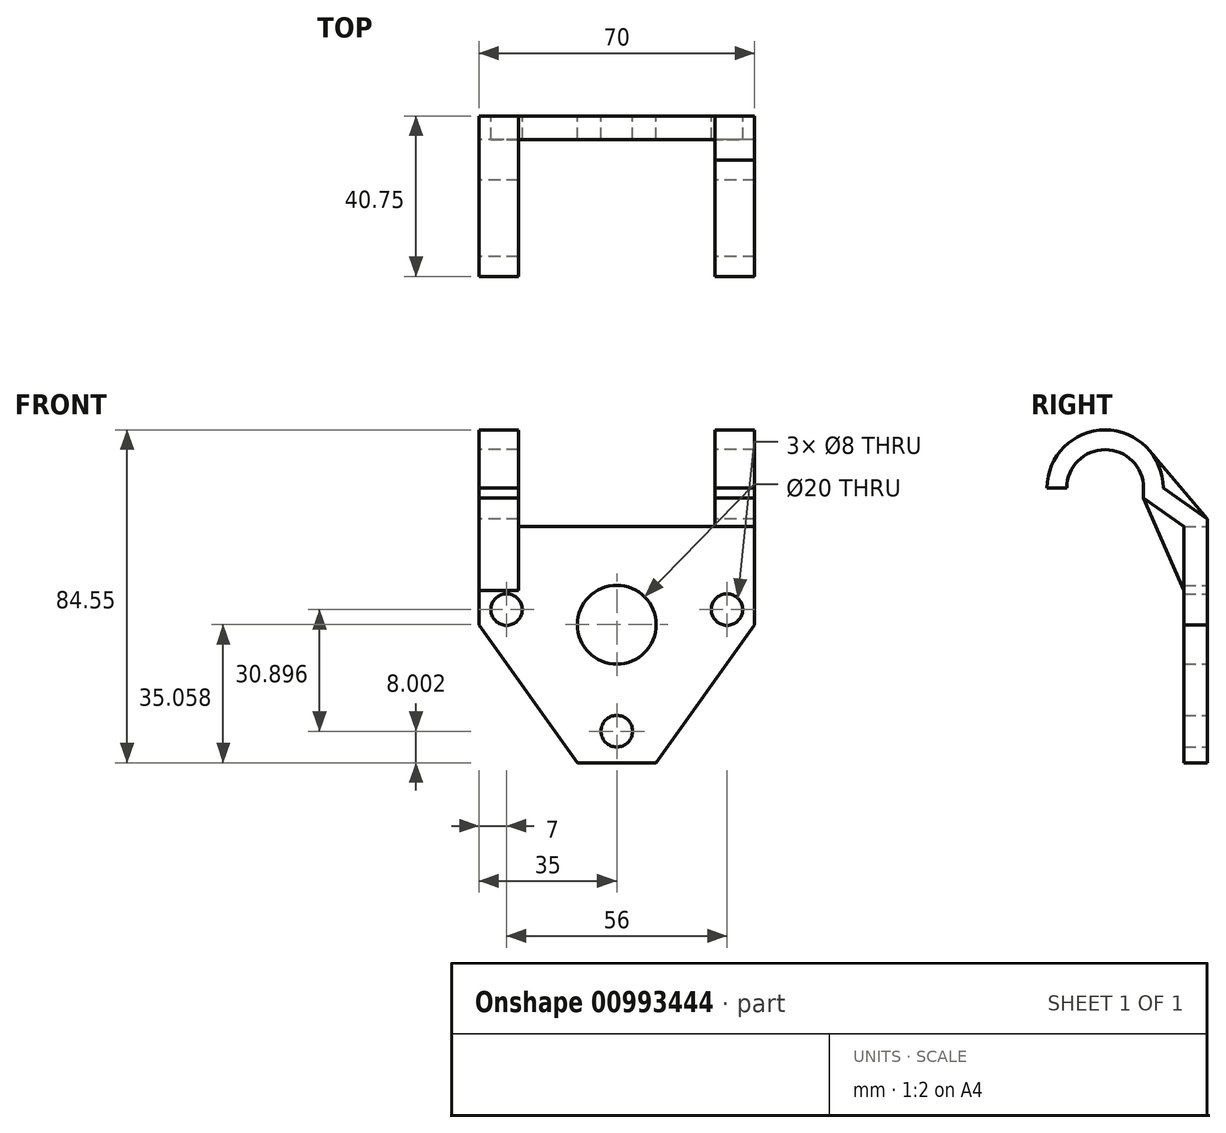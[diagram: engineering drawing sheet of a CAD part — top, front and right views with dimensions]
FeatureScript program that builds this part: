
annotation { "Feature Type Name" : "Feature", "Feature Type Description" : "" }
export const myFeature = defineFeature(function(context is Context, id is Id, definition is map)
    precondition{}
    {
        {
            var Q0;
            Q0=qCreatedBy(makeId("Right.planeOp"),FACE);
            var sketch = newSketch(context, id + "F0", { "sketchPlane" : qUnion([Q0])});
            skArc(sketch, "E0", {"start": v(9.75, 0) * mm, "mid": v(0, 9.75) * mm, "end": v(-9.75, 0) * mm});
            skArc(sketch, "E1.0", {"start": v(14.75, 0) * mm, "mid": v(0, 14.75) * mm, "end": v(-14.75, 0) * mm});
            skLineSegment(sketch, "E2.trimOffspring", {"start": v(-9.75, 0) * mm, "end": v(-14.75, 0) * mm});
            skPoint(sketch, "E3", {"position": v(0, 14.75) * mm});
            skLineSegment(sketch, "E4", {"start": v(14.75, 0) * mm, "end": v(26, -7.9) * mm});
            skLineSegment(sketch, "E5", {"start": v(9.75, -2.6) * mm, "end": v(20, -9.8) * mm});
            skLineSegment(sketch, "E6", {"start": v(9.75, -2.6) * mm, "end": v(9.75, 0) * mm});
            skLineSegment(sketch, "E7", {"start": v(20, -9.8) * mm, "end": v(20, -69.8) * mm});
            skLineSegment(sketch, "E8", {"start": v(26, -7.9) * mm, "end": v(26, -69.8) * mm});
            skLineSegment(sketch, "E9", {"start": v(20, -69.8) * mm, "end": v(26, -69.8) * mm});
            skSolve(sketch);
        }
        {
            var Q0;
            Q0 = qSketchRegion(id + "F0", true);
            extrude(context, id + "F1", {"entities" : qUnion([Q0]), "depth" : 70 * mm, "offsetDistance" : 25 * mm});
        }
        {
            var Q0;
            Q0=makeQuery(id+"F1.opExtrude","CAP_FACE",FACE,{"disambiguationData":[OSD([sQuery(id+"F0.wireOp",EDGE,"E0"),sQuery(id+"F0.wireOp",EDGE,"E1.0"),sQuery(id+"F0.wireOp",EDGE,"E2.trimOffspring"),sQuery(id+"F0.wireOp",EDGE,"E4"),sQuery(id+"F0.wireOp",EDGE,"E5"),sQuery(id+"F0.wireOp",EDGE,"E6"),sQuery(id+"F0.wireOp",EDGE,"E7"),sQuery(id+"F0.wireOp",EDGE,"E8"),sQuery(id+"F0.wireOp",EDGE,"E9")])],"isStart":false});
            var sketch = newSketch(context, id + "F2", { "sketchPlane" : qUnion([Q0])});
            skPoint(sketch, "E10", {"position": v(0, 14.75) * mm});
            skSolve(sketch);
        }
        {
            var Q0;
            Q0=makeQuery(id+"F1.opExtrude","CAP_FACE",FACE,{"disambiguationData":[OSD([sQuery(id+"F0.wireOp",EDGE,"E0"),sQuery(id+"F0.wireOp",EDGE,"E1.0"),sQuery(id+"F0.wireOp",EDGE,"E2.trimOffspring"),sQuery(id+"F0.wireOp",EDGE,"E4"),sQuery(id+"F0.wireOp",EDGE,"E5"),sQuery(id+"F0.wireOp",EDGE,"E6"),sQuery(id+"F0.wireOp",EDGE,"E7"),sQuery(id+"F0.wireOp",EDGE,"E8"),sQuery(id+"F0.wireOp",EDGE,"E9")])],"isStart":true});
            var sketch = newSketch(context, id + "F3", { "sketchPlane" : qUnion([Q0])});
            skPoint(sketch, "E11", {"position": v(0, 14.75) * mm});
            skSolve(sketch);
        }
        {
            var Q0;
            Q0=makeQuery(id+"F1.opExtrude","SWEPT_FACE",FACE,{"disambiguationData":[OSD([sQuery(id+"F0.wireOp",EDGE,"E8")])]});
            var sketch = newSketch(context, id + "F4", { "sketchPlane" : qUnion([Q0])});
            skLineSegment(sketch, "E12", {"start": v(-70, -34.8) * mm, "end": v(-45, -69.8) * mm});
            skLineSegment(sketch, "E13", {"start": v(-45, -69.8) * mm, "end": v(-25, -69.8) * mm});
            skLineSegment(sketch, "E14", {"start": v(-25, -69.8) * mm, "end": v(0, -34.8) * mm});
            skLineSegment(sketch, "E15", {"start": v(-70, -34.8) * mm, "end": v(-90, -34.8) * mm});
            skLineSegment(sketch, "E16", {"start": v(-90, -34.8) * mm, "end": v(-90, -94.8) * mm});
            skLineSegment(sketch, "E17", {"start": v(-90, -94.8) * mm, "end": v(20, -94.8) * mm});
            skLineSegment(sketch, "E18", {"start": v(20, -94.8) * mm, "end": v(20, -34.8) * mm});
            skLineSegment(sketch, "E19", {"start": v(20, -34.8) * mm, "end": v(0, -34.8) * mm});
            skLineSegment(sketch, "E20", {"start": v(-60, -9.8) * mm, "end": v(-10, -9.8) * mm});
            skLineSegment(sketch, "E21", {"start": v(-60, -9.8) * mm, "end": v(-60, 14.75) * mm});
            skLineSegment(sketch, "E22", {"start": v(-60, 14.75) * mm, "end": v(-10, 14.75) * mm});
            skLineSegment(sketch, "E23", {"start": v(-10, 14.75) * mm, "end": v(-10, -9.8) * mm});
            skSolve(sketch);
        }
        {
            var Q0;
            Q0 = qSketchRegion(id + "F4", true);
            extrude(context, id + "F5", {"entities" : qUnion([Q0]), "operationType" : NewBodyOperationType.REMOVE, "oppositeDirection" : true, "depth" : 25 * mm, "offsetDistance" : 25 * mm});
        }
        {
            var Q0;
            Q0=makeQuery(id+"F1.opExtrude","SWEPT_FACE",FACE,{"disambiguationData":[OSD([sQuery(id+"F0.wireOp",EDGE,"E8")])]});
            var sketch = newSketch(context, id + "F6", { "sketchPlane" : qUnion([Q0])});
            skCircle(sketch, "E24", {"center": v(-63, -30.9) * mm, "radius": 4 * mm});
            skCircle(sketch, "E25", {"center": v(-7, -30.9) * mm, "radius": 4 * mm});
            skSolve(sketch);
        }
        {
            var Q0;
            Q0 = qSketchRegion(id + "F4", true);
            extrude(context, id + "F7", {"entities" : qUnion([Q0]), "operationType" : NewBodyOperationType.REMOVE, "endBound" : BoundingType.THROUGH_ALL, "oppositeDirection" : true, "depth" : 25 * mm, "offsetDistance" : 25 * mm});
        }
        {
            var Q0;
            Q0=makeQuery(id+"F6.imprint","IMPRINT",FACE,{"disambiguationData":[TD([[makeQuery(id+"F6.imprint","IMPRINT",EDGE,{"derivedFrom":sQuery(id+"F6.wireOp",EDGE,"E25")}),-1.0]])]});
            var sketch = newSketch(context, id + "F8", { "sketchPlane" : qUnion([Q0])});
            skCircle(sketch, "E26", {"center": v(-35, -34.74) * mm, "radius": 10 * mm});
            skSolve(sketch);
        }
        {
            var Q0;
            Q0 = qSketchRegion(id + "F8", true);
            extrude(context, id + "F9", {"entities" : qUnion([Q0]), "operationType" : NewBodyOperationType.REMOVE, "endBound" : BoundingType.THROUGH_ALL, "oppositeDirection" : true, "depth" : 2.5 * mm, "offsetDistance" : 25 * mm});
        }
        {
            var Q0;
            Q0=makeQuery(id+"F6.imprint","IMPRINT",FACE,{"disambiguationData":[TD([[makeQuery(id+"F6.imprint","IMPRINT",EDGE,{"derivedFrom":sQuery(id+"F6.wireOp",EDGE,"E25")}),-1.0]])]});
            var sketch = newSketch(context, id + "F10", { "sketchPlane" : qUnion([Q0])});
            skCircle(sketch, "E27", {"center": v(-35, -34.74) * mm, "radius": 6.38 * mm});
            skSolve(sketch);
        }
        {
            var Q0;
            Q0 = qSketchRegion(id + "F10", true);
            extrude(context, id + "F11", {"entities" : qUnion([Q0]), "operationType" : NewBodyOperationType.REMOVE, "endBound" : BoundingType.THROUGH_ALL, "oppositeDirection" : true, "depth" : 25 * mm, "offsetDistance" : 25 * mm});
        }
        {
            var Q0;
            Q0 = qSketchRegion(id + "F6", true);
            extrude(context, id + "F12", {"entities" : qUnion([Q0]), "operationType" : NewBodyOperationType.REMOVE, "endBound" : BoundingType.THROUGH_ALL, "oppositeDirection" : true, "depth" : 25 * mm, "offsetDistance" : 25 * mm});
        }
        {
            var Q0;
            Q0=qCreatedBy(makeId("Right.planeOp"),FACE);
            cPlane(context, id + "F13", {"entities" : qUnion([Q0]), "cplaneType" : CPlaneType.OFFSET, "offset" : 35 * mm, "width" : 150 * mm, "height" : 150 * mm});
        }
        {
            var Q0;
            Q0=makeQuery(id+"F3.imprint","IMPRINT",FACE,{"disambiguationData":[TD([[makeQuery(id+"F3.imprint","IMPRINT",EDGE,{"derivedFrom":makeQuery(id+"F1.opExtrude","CAP_EDGE",EDGE,{"disambiguationData":[OSD([sQuery(id+"F0.wireOp",EDGE,"E0")])],"isStart":true})}),1.0]])]});
            var sketch = newSketch(context, id + "F14", { "sketchPlane" : qUnion([Q0])});
            skLineSegment(sketch, "E28", {"start": v(-20, -26) * mm, "end": v(-9.75, -2.6) * mm});
            skLineSegment(sketch, "E29", {"start": v(-9.75, -2.6) * mm, "end": v(-20, -9.8) * mm});
            skLineSegment(sketch, "E30", {"start": v(-20, -9.8) * mm, "end": v(-20, -26) * mm});
            skSolve(sketch);
        }
        {
            var Q0;
            Q0 = qSketchRegion(id + "F14", true);
            extrude(context, id + "F15", {"entities" : qUnion([Q0]), "operationType" : NewBodyOperationType.ADD, "oppositeDirection" : true, "depth" : 10 * mm, "offsetDistance" : 25 * mm});
        }
        {
            var Q0;
            Q0=makeQuery(id+"F1.opExtrude","SWEPT_FACE",FACE,{"disambiguationData":[OSD([sQuery(id+"F0.wireOp",EDGE,"E8")])]});
            var sketch = newSketch(context, id + "F16", { "sketchPlane" : qUnion([Q0])});
            skCircle(sketch, "E31", {"center": v(-35, -61.8) * mm, "radius": 4 * mm});
            skSolve(sketch);
        }
        {
            var Q0;
            Q0 = qSketchRegion(id + "F16", true);
            extrude(context, id + "F17", {"entities" : qUnion([Q0]), "operationType" : NewBodyOperationType.REMOVE, "endBound" : BoundingType.THROUGH_ALL, "oppositeDirection" : true, "depth" : 25 * mm, "offsetDistance" : 25 * mm});
        }
        {
            var Q0;
            Q0=makeQuery(id+"F3.imprint","IMPRINT",FACE,{"disambiguationData":[TD([[makeQuery(id+"F3.imprint","IMPRINT",EDGE,{"derivedFrom":makeQuery(id+"F1.opExtrude","CAP_EDGE",EDGE,{"disambiguationData":[OSD([sQuery(id+"F0.wireOp",EDGE,"E0")])],"isStart":true})}),1.0]])]});
            var sketch = newSketch(context, id + "F18", { "sketchPlane" : qUnion([Q0])});
            skLineSegment(sketch, "E32", {"start": v(-26, -7.9) * mm, "end": v(-11.26, 9.52) * mm});
            skLineSegment(sketch, "E33", {"start": v(-11.26, 9.52) * mm, "end": v(-14.75, 0) * mm});
            skLineSegment(sketch, "E34", {"start": v(-26, -7.9) * mm, "end": v(-14.75, 0) * mm});
            skSolve(sketch);
        }
        {
            var Q0;
            Q0 = qSketchRegion(id + "F18", true);
            extrude(context, id + "F19", {"entities" : qUnion([Q0]), "operationType" : NewBodyOperationType.ADD, "oppositeDirection" : true, "depth" : 10 * mm, "offsetDistance" : 25 * mm});
        }
    });
